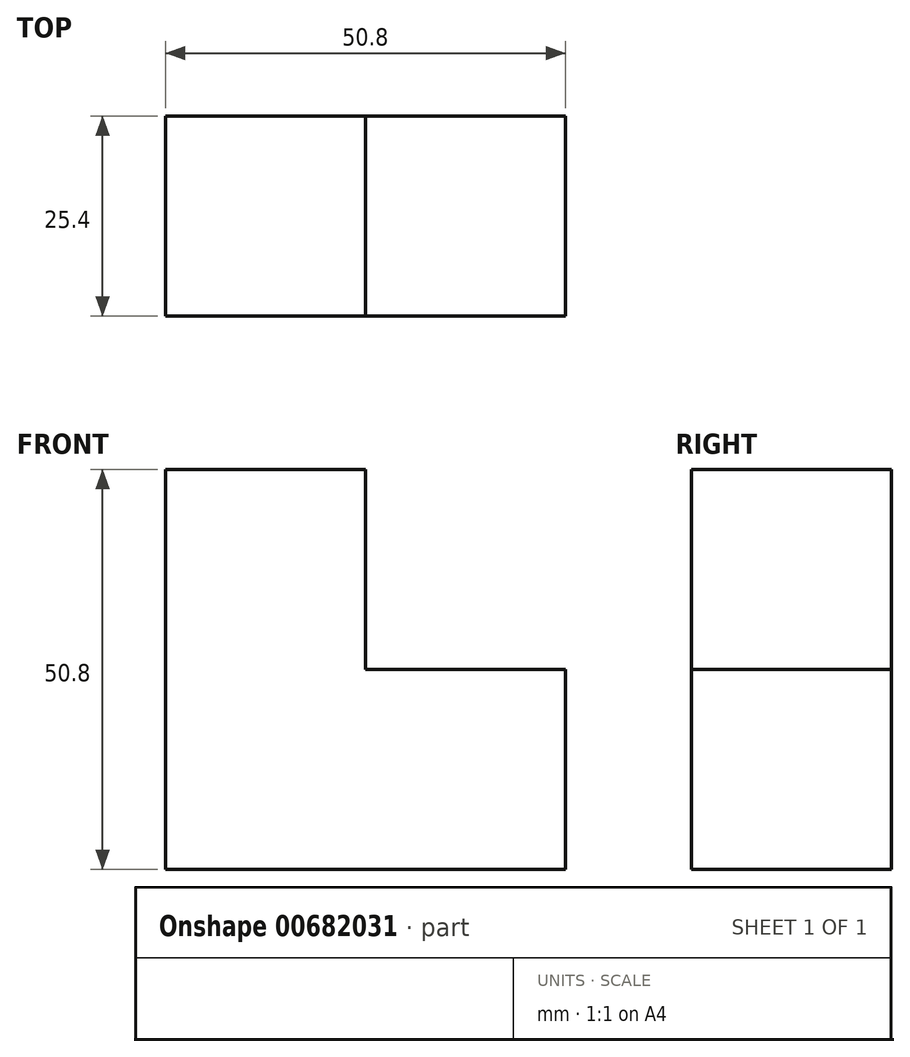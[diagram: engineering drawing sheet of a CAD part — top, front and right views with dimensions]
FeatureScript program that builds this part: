
annotation { "Feature Type Name" : "Feature", "Feature Type Description" : "" }
export const myFeature = defineFeature(function(context is Context, id is Id, definition is map)
    precondition{}
    {
        {
            var Q0;
            Q0=qCreatedBy(makeId("Front.planeOp"),FACE);
            var sketch = newSketch(context, id + "F0", { "sketchPlane" : qUnion([Q0])});
            skLineSegment(sketch, "E0", {"start": v(-50.8, 50.8) * mm, "end": v(-50.8, 0) * mm});
            skLineSegment(sketch, "E1", {"start": v(-50.8, 0) * mm, "end": v(0, 0) * mm});
            skLineSegment(sketch, "E2", {"start": v(0, 0) * mm, "end": v(0, 25.4) * mm});
            skLineSegment(sketch, "E3", {"start": v(0, 25.4) * mm, "end": v(-25.4, 25.4) * mm});
            skLineSegment(sketch, "E4", {"start": v(-25.4, 25.4) * mm, "end": v(-25.4, 50.8) * mm});
            skLineSegment(sketch, "E5", {"start": v(-25.4, 50.8) * mm, "end": v(-50.8, 50.8) * mm});
            skSolve(sketch);
        }
        {
            var Q0;
            Q0 = qSketchRegion(id + "F0", true);
            extrude(context, id + "F1", {"entities" : qUnion([Q0]), "depth" : 25.4 * mm, "offsetDistance" : 25.4 * mm});
        }
    });
